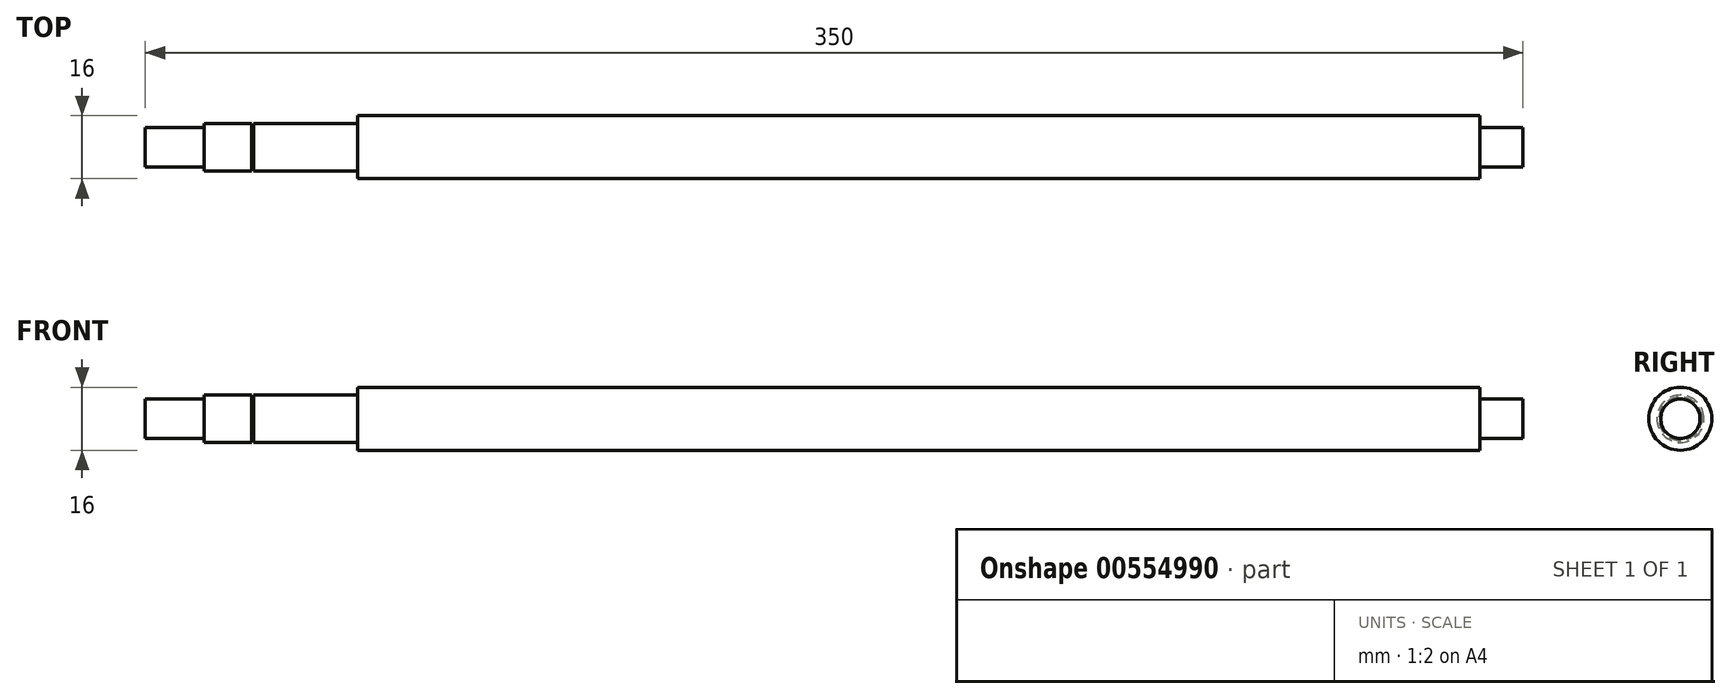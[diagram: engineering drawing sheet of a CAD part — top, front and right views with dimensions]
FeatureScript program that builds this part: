
annotation { "Feature Type Name" : "Feature", "Feature Type Description" : "" }
export const myFeature = defineFeature(function(context is Context, id is Id, definition is map)
    precondition{}
    {
        {
            var Q0;
            Q0=qCreatedBy(makeId("Front.planeOp"),FACE);
            var sketch = newSketch(context, id + "F0", { "sketchPlane" : qUnion([Q0])});
            skLineSegment(sketch, "E0.bottom", {"start": v(-142.5, 0) * mm, "end": v(142.5, 0) * mm});
            skLineSegment(sketch, "E0.top", {"start": v(-142.5, 8) * mm, "end": v(142.5, 8) * mm});
            skLineSegment(sketch, "E0.left", {"start": v(-142.5, 0) * mm, "end": v(-142.5, 8) * mm});
            skLineSegment(sketch, "E0.right", {"start": v(142.5, 0) * mm, "end": v(142.5, 8) * mm});
            skLineSegment(sketch, "E1.bottom", {"start": v(142.5, 5) * mm, "end": v(153.5, 5) * mm});
            skLineSegment(sketch, "E1.top", {"start": v(142.5, 0) * mm, "end": v(153.5, 0) * mm});
            skLineSegment(sketch, "E1.left", {"start": v(142.5, 5) * mm, "end": v(142.5, 0) * mm});
            skLineSegment(sketch, "E1.right", {"start": v(153.5, 5) * mm, "end": v(153.5, 0) * mm});
            skLineSegment(sketch, "E2.bottom", {"start": v(-142.5, 6) * mm, "end": v(-169, 6) * mm});
            skLineSegment(sketch, "E2.top", {"start": v(-142.5, 0) * mm, "end": v(-181.5, 0) * mm});
            skLineSegment(sketch, "E2.left", {"start": v(-142.5, 6) * mm, "end": v(-142.5, 0) * mm});
            skLineSegment(sketch, "E2.right", {"start": v(-181.5, 6) * mm, "end": v(-181.5, 0) * mm});
            skLineSegment(sketch, "E3.bottom", {"start": v(-181.5, 5) * mm, "end": v(-196.5, 5) * mm});
            skLineSegment(sketch, "E3.top", {"start": v(-181.5, 0) * mm, "end": v(-196.5, 0) * mm});
            skLineSegment(sketch, "E3.left", {"start": v(-181.5, 5) * mm, "end": v(-181.5, 0) * mm});
            skLineSegment(sketch, "E3.right", {"start": v(-196.5, 5) * mm, "end": v(-196.5, 0) * mm});
            skLineSegment(sketch, "E4", {"start": v(-169.5, 6) * mm, "end": v(-169.5, 5.5) * mm});
            skLineSegment(sketch, "E5", {"start": v(-169.5, 5.5) * mm, "end": v(-169, 5.5) * mm});
            skLineSegment(sketch, "E6", {"start": v(-169, 5.5) * mm, "end": v(-169, 6) * mm});
            skLineSegment(sketch, "E7.trimOffspring", {"start": v(-169.5, 6) * mm, "end": v(-181.5, 6) * mm});
            skSolve(sketch);
        }
        {
            var Q0;
            Q0 = qSketchRegion(id + "F0", true);
            var Q1;
            Q1=sQuery(id+"F0.wireOp",EDGE,"E0.bottom");
            revolve(context, id + "F1", {"entities" : qUnion([Q0]), "axis" : qUnion([Q1]), "revolveType" : RevolveType.FULL});
        }
    });
